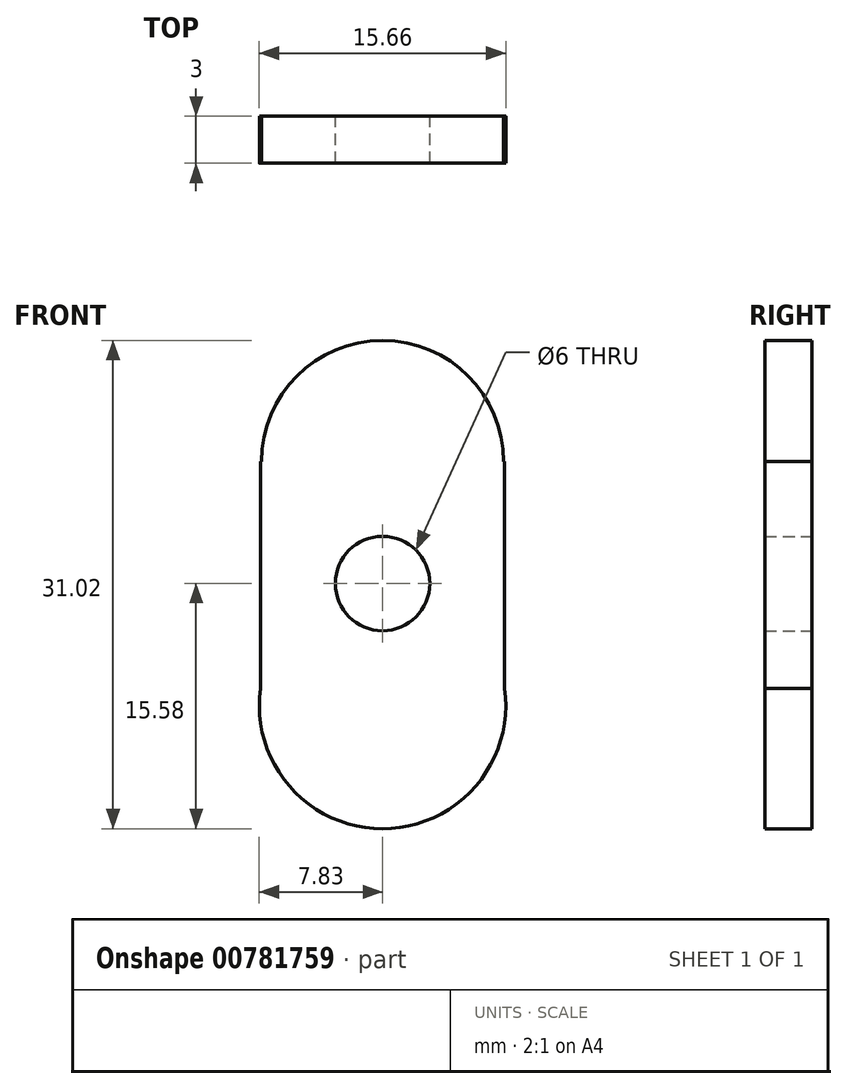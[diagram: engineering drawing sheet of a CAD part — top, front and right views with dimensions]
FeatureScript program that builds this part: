
annotation { "Feature Type Name" : "Feature", "Feature Type Description" : "" }
export const myFeature = defineFeature(function(context is Context, id is Id, definition is map)
    precondition{}
    {
        {
            var Q0;
            Q0=qCreatedBy(makeId("Front.planeOp"),FACE);
            var sketch = newSketch(context, id + "F0", { "sketchPlane" : qUnion([Q0])});
            skLineSegment(sketch, "E0.top", {"start": v(7.75, 7.75) * mm, "end": v(7.7, 7.75) * mm});
            skLineSegment(sketch, "E0.left", {"start": v(7.75, -7.75) * mm, "end": v(7.75, 7.75) * mm});
            skLineSegment(sketch, "E0.right", {"start": v(-7.75, -7.75) * mm, "end": v(-7.75, 7.75) * mm});
            skArc(sketch, "E1", {"start": v(-0.4, 0.07) * mm, "mid": v(0, 0.06) * mm, "end": v(0.4, 0.07) * mm});
            skArc(sketch, "E2", {"start": v(-7.75, -6.66) * mm, "mid": v(0, -15.58) * mm, "end": v(7.75, -6.66) * mm});
            skLineSegment(sketch, "E3.trimOffspring", {"start": v(-7.7, 7.75) * mm, "end": v(-7.75, 7.75) * mm});
            skArc(sketch, "E4.trimOffspring", {"start": v(7.7, 7.75) * mm, "mid": v(0, 15.44) * mm, "end": v(-7.7, 7.75) * mm});
            skArc(sketch, "E5.trimOffspring", {"start": v(0.4, 0.07) * mm, "mid": v(0, 0.08) * mm, "end": v(-0.4, 0.07) * mm});
            skCircle(sketch, "E6", {"center": v(0, 0) * mm, "radius": 3 * mm});
            skSolve(sketch);
        }
        {
            var Q0;
            {var subQ4=sQuery(id+"F0.wireOp",EDGE,"E0.top");Q0=makeQuery(id+"F0.imprint","IMPRINT",FACE,{"disambiguationData":[TD([[makeQuery(id+"F0.imprint","IMPRINT",EDGE,{"derivedFrom":subQ4}),1.0]])]});}
            extrude(context, id + "F1", {"entities" : qUnion([Q0]), "depth" : 3 * mm, "offsetDistance" : 25 * mm});
        }
    });
